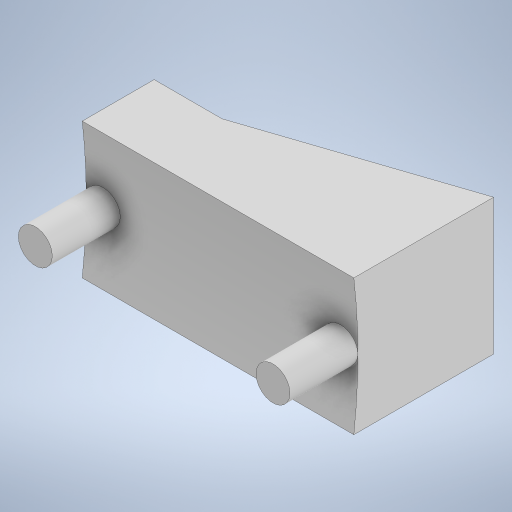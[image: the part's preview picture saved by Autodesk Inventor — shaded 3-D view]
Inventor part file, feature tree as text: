
AUTODESK INVENTOR PART (.ipt)
format: ipt  version: 2023 (Build 270158000, 158)  size: 244,224 bytes
history: native  units: in
note: dims shown in document units (in); Inventor stores cm internally (conversion verified against a paired STEP export)
features: extrude x4, sketch x4, plane x1
ambient origin geometry x8: Origin, YZ Plane, XZ Plane, XY Plane, X Axis, Y Axis, Z Axis, Center Point
bodies: Solid1 (feature_tree)
feature tree (9):
  extrude  "Extrusion1"  Depth=0.0787in
  extrude  "Extrusion2"  Depth=0.1575in
  plane  "Work Plane1"
  extrude  "Extrusion3"  Depth=0.0394in
  extrude  "Extrusion4"  TaperAngle=0.0deg  [1 undecoded]
  sketch  "Sketch1"  dims[d0=0.0394in d1=0.0787in]
  sketch  "Sketch2"  dims[d2=0.0394in d3=0.1575in]
  sketch  "Sketch3"  dims[d4=0.0787in d5=0.0in d6=0.0394in]
  sketch  "Sketch4"  dims[d7=0.3346in d8=0.0in d9=0.1088in d10=0.0in d11=0.0197in d12=0.0394in d13=0.0in d14=0.0197in d15=0.0394in d16=0.0in]
note: 1 required parameter value undecoded (feature->parameter linkage not recoverable at this tier; creation-order binding heuristic only, values carry confidence <= 0.55)
